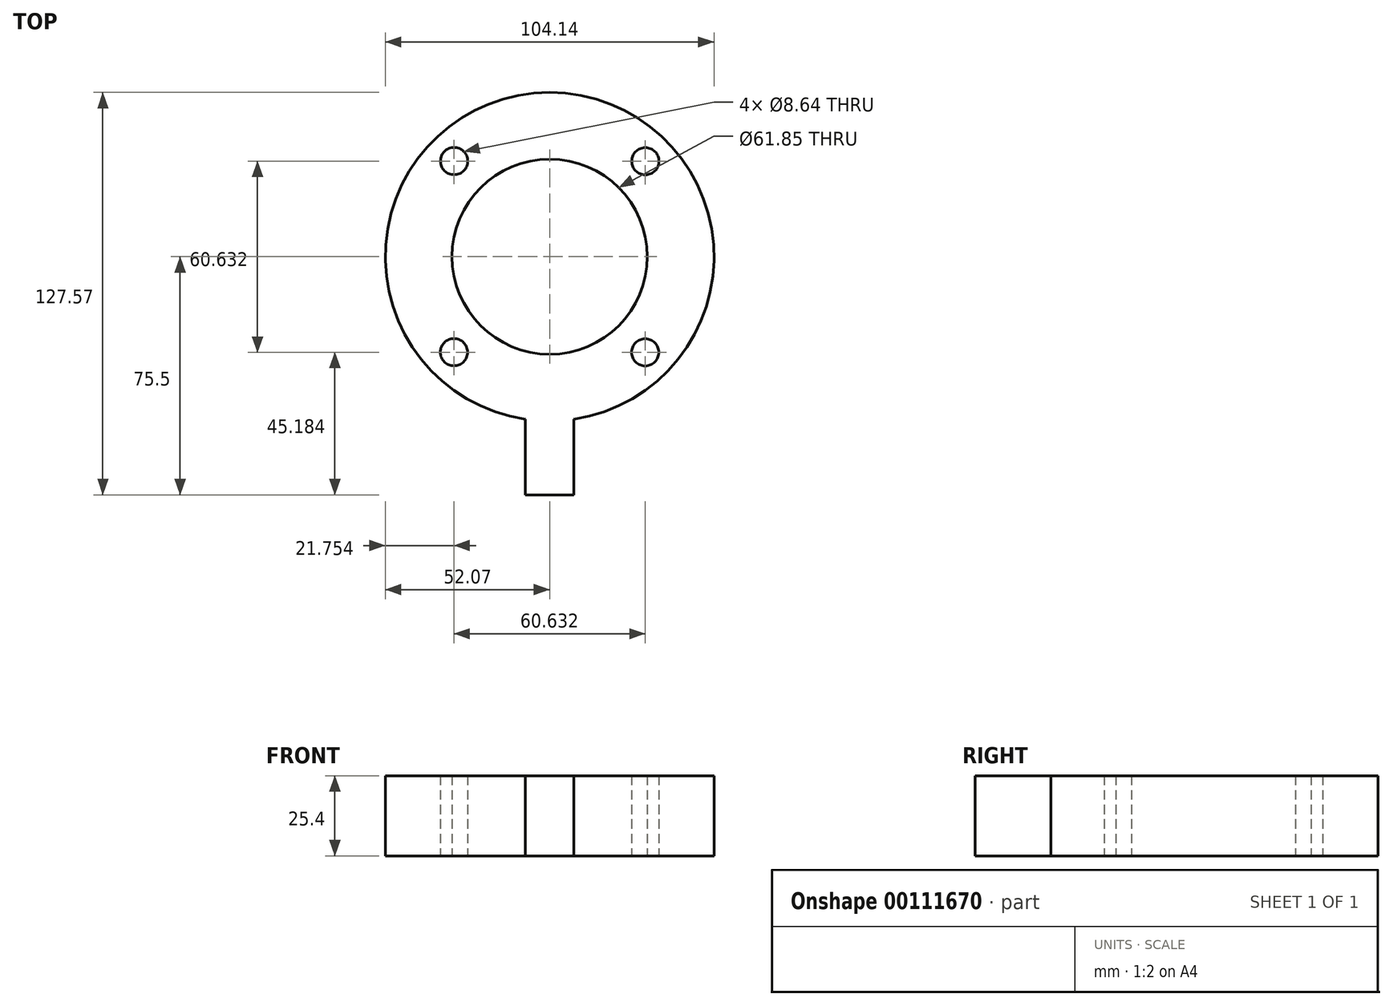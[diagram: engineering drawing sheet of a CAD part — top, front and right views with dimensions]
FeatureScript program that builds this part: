
annotation { "Feature Type Name" : "Feature", "Feature Type Description" : "" }
export const myFeature = defineFeature(function(context is Context, id is Id, definition is map)
    precondition{}
    {
        {
            var Q0;
            Q0=qCreatedBy(makeId("Top.planeOp"),FACE);
            var sketch = newSketch(context, id + "F0", { "sketchPlane" : qUnion([Q0])});
            skArc(sketch, "E0", {"start": v(7.65, -51.5) * mm, "mid": v(0, 52.07) * mm, "end": v(-7.65, -51.5) * mm});
            skCircle(sketch, "E1", {"center": v(0, 0) * mm, "radius": 30.92 * mm});
            skCircle(sketch, "E2", {"center": v(0, 0) * mm, "radius": 42.84 * mm, "construction": true});
            skLineSegment(sketch, "E3", {"start": v(0, 0) * mm, "end": v(-72.25, 72.37) * mm, "construction": true});
            skLineSegment(sketch, "E4", {"start": v(0, 0) * mm, "end": v(0, -63.5) * mm, "construction": true});
            skLineSegment(sketch, "E5.top", {"start": v(-7.65, -75.5) * mm, "end": v(7.65, -75.5) * mm});
            skLineSegment(sketch, "E5.left", {"start": v(-7.65, -51.5) * mm, "end": v(-7.65, -75.5) * mm});
            skLineSegment(sketch, "E5.right", {"start": v(7.65, -51.5) * mm, "end": v(7.65, -75.5) * mm});
            skPoint(sketch, "E5.middle", {"position": v(0, -63.5) * mm});
            skCircle(sketch, "E6", {"center": v(-30.26, 30.32) * mm, "radius": 4.32 * mm});
            skCircle(sketch, "E7.1.0", {"center": v(-30.32, -30.26) * mm, "radius": 4.32 * mm});
            skCircle(sketch, "E7.2.0", {"center": v(30.26, -30.32) * mm, "radius": 4.32 * mm});
            skCircle(sketch, "E7.3.0", {"center": v(30.32, 30.26) * mm, "radius": 4.32 * mm});
            skSolve(sketch);
        }
        {
            var Q0;
            Q0=makeQuery(id+"F0.imprint","IMPRINT",FACE,{"disambiguationData":[TD([[makeQuery(id+"F0.imprint","IMPRINT",EDGE,{"derivedFrom":sQuery(id+"F0.wireOp",EDGE,"E0")}),1.0]])]});
            extrude(context, id + "F1", {"entities" : qUnion([Q0]), "depth" : 25.4 * mm});
        }
    });
